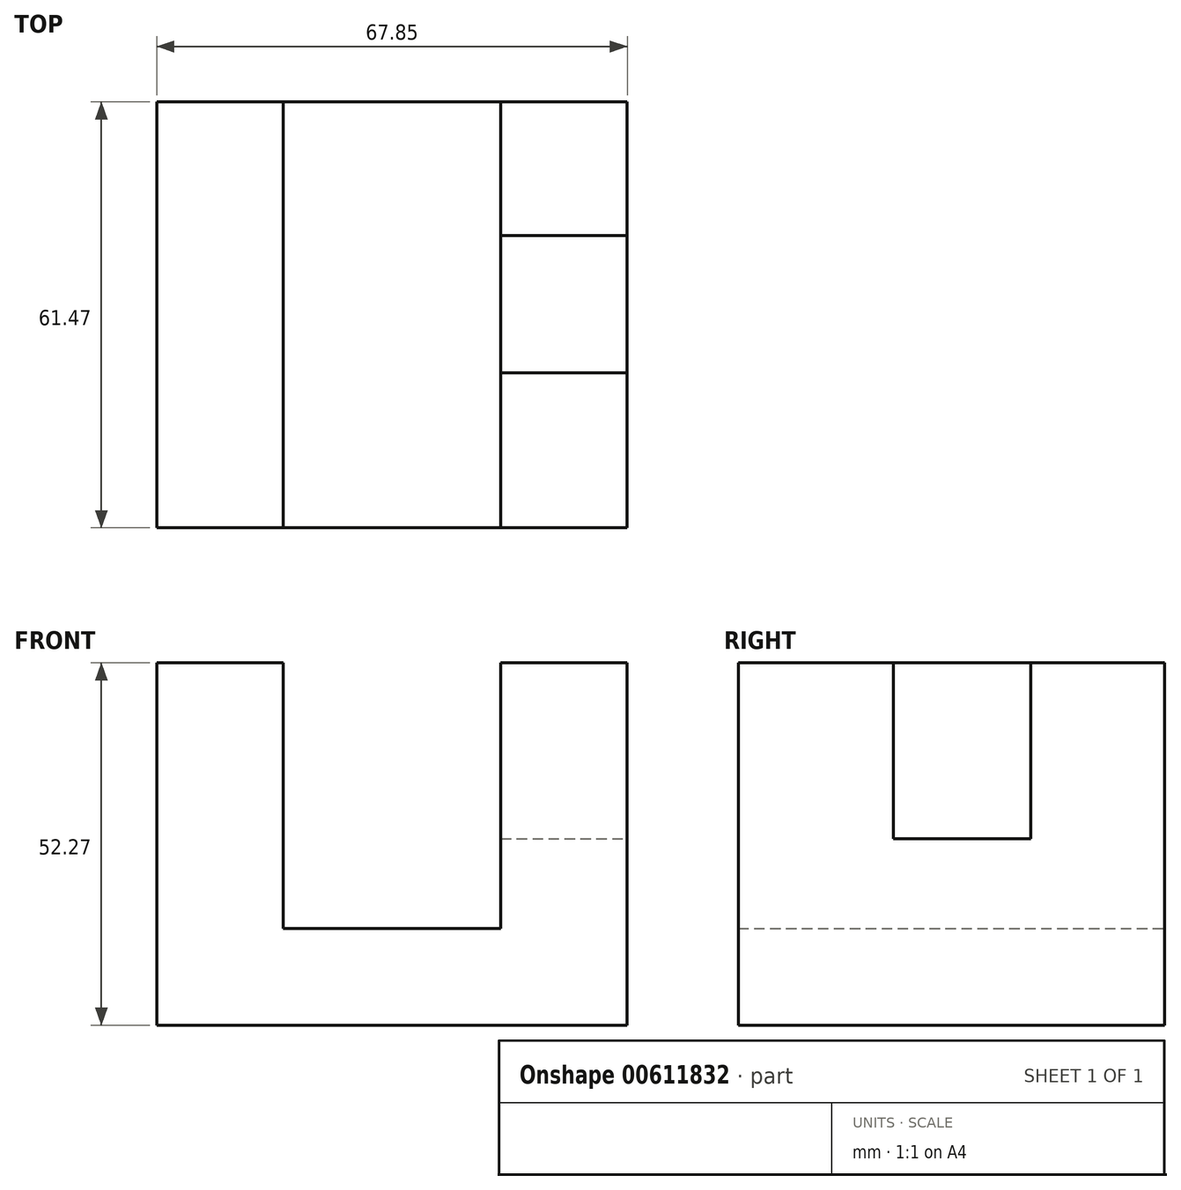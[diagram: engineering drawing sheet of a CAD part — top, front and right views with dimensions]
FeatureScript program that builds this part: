
annotation { "Feature Type Name" : "Feature", "Feature Type Description" : "" }
export const myFeature = defineFeature(function(context is Context, id is Id, definition is map)
    precondition{}
    {
        {
            var Q0;
            Q0=qCreatedBy(makeId("Front.planeOp"),FACE);
            var sketch = newSketch(context, id + "F0", { "sketchPlane" : qUnion([Q0])});
            skLineSegment(sketch, "E0.bottom", {"start": v(0, 0) * mm, "end": v(67.85, 0) * mm});
            skLineSegment(sketch, "E0.top", {"start": v(0, 52.27) * mm, "end": v(18.25, 52.27) * mm});
            skLineSegment(sketch, "E0.left", {"start": v(0, 0) * mm, "end": v(0, 52.27) * mm});
            skLineSegment(sketch, "E0.right", {"start": v(67.85, 0) * mm, "end": v(67.85, 52.27) * mm});
            skLineSegment(sketch, "E1.top", {"start": v(18.25, 13.92) * mm, "end": v(49.6, 13.92) * mm});
            skLineSegment(sketch, "E1.left", {"start": v(18.25, 52.27) * mm, "end": v(18.25, 13.92) * mm});
            skLineSegment(sketch, "E1.right", {"start": v(49.6, 52.27) * mm, "end": v(49.6, 13.92) * mm});
            skLineSegment(sketch, "E2.trimOffspring", {"start": v(49.6, 52.27) * mm, "end": v(67.85, 52.27) * mm});
            skSolve(sketch);
        }
        {
            var Q0;
            Q0 = qSketchRegion(id + "F0", true);
            extrude(context, id + "F1", {"entities" : qUnion([Q0]), "depth" : 61.47 * mm, "offsetDistance" : 25.4 * mm});
        }
        {
            var Q0;
            Q0=makeQuery(id+"F1.opExtrude","SWEPT_FACE",FACE,{"disambiguationData":[OSD([sQuery(id+"F0.wireOp",EDGE,"E2.trimOffspring")])]});
            var sketch = newSketch(context, id + "F2", { "sketchPlane" : qUnion([Q0])});
            skLineSegment(sketch, "E3.bottom", {"start": v(49.6, -19.27) * mm, "end": v(67.85, -19.27) * mm});
            skLineSegment(sketch, "E3.top", {"start": v(49.6, -39.07) * mm, "end": v(67.85, -39.07) * mm});
            skLineSegment(sketch, "E3.left", {"start": v(49.6, -19.27) * mm, "end": v(49.6, -39.07) * mm});
            skLineSegment(sketch, "E3.right", {"start": v(67.85, -19.27) * mm, "end": v(67.85, -39.07) * mm});
            skSolve(sketch);
        }
        {
            var Q0;
            Q0=makeQuery(id+"F2.imprint","IMPRINT",FACE,{"disambiguationData":[TD([[makeQuery(id+"F2.imprint","IMPRINT",EDGE,{"derivedFrom":sQuery(id+"F2.wireOp",EDGE,"E3.bottom")}),-1.0]])]});
            extrude(context, id + "F3", {"entities" : qUnion([Q0]), "operationType" : NewBodyOperationType.REMOVE, "oppositeDirection" : true, "depth" : 25.4 * mm, "offsetDistance" : 25.4 * mm});
        }
    });
